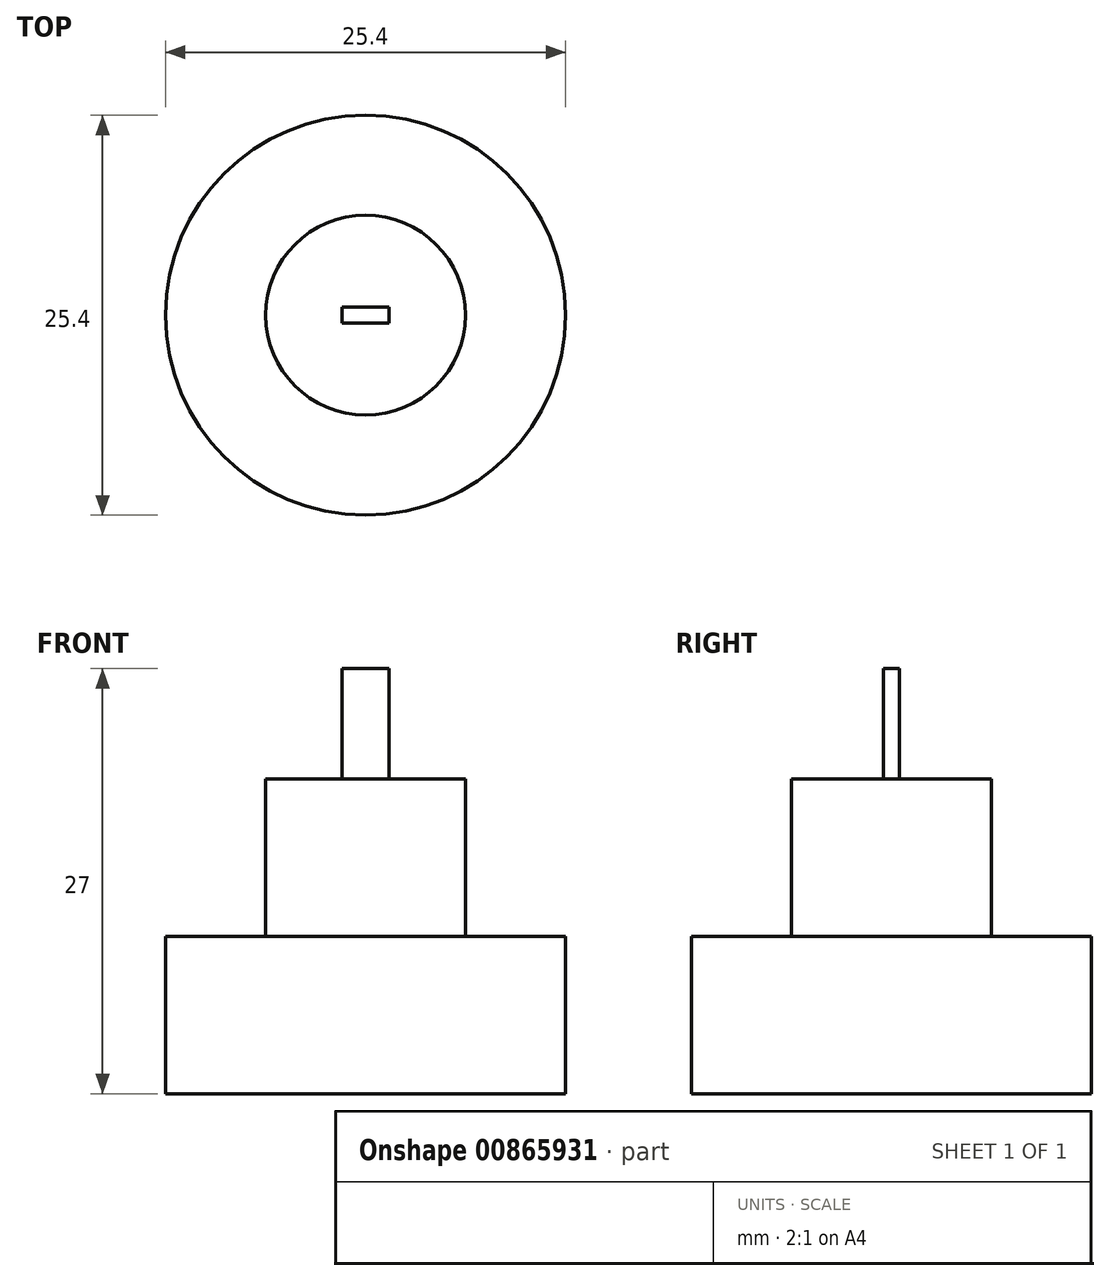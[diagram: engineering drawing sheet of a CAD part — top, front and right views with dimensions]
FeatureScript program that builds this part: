
annotation { "Feature Type Name" : "Feature", "Feature Type Description" : "" }
export const myFeature = defineFeature(function(context is Context, id is Id, definition is map)
    precondition{}
    {
        {
            var Q0;
            Q0=qCreatedBy(makeId("Top.planeOp"),FACE);
            var sketch = newSketch(context, id + "F0", { "sketchPlane" : qUnion([Q0])});
            skCircle(sketch, "E0", {"center": v(0, 0) * mm, "radius": 12.7 * mm});
            skCircle(sketch, "E1", {"center": v(0, 0) * mm, "radius": 6.35 * mm});
            skSolve(sketch);
        }
        {
            var Q0;
            Q0=makeQuery(id+"F0.imprint","IMPRINT",FACE,{"disambiguationData":[TD([[makeQuery(id+"F0.imprint","IMPRINT",EDGE,{"derivedFrom":sQuery(id+"F0.wireOp",EDGE,"E0")}),1.0]])]});
            extrude(context, id + "F1", {"entities" : qUnion([Q0]), "depth" : 10 * mm, "offsetDistance" : 25 * mm});
        }
        {
            var Q0;
            Q0=makeQuery(id+"F0.imprint","IMPRINT",FACE,{"disambiguationData":[TD([[makeQuery(id+"F0.imprint","IMPRINT",EDGE,{"derivedFrom":sQuery(id+"F0.wireOp",EDGE,"E1")}),1.0]])]});
            extrude(context, id + "F2", {"entities" : qUnion([Q0]), "operationType" : NewBodyOperationType.ADD, "depth" : 20 * mm, "offsetDistance" : 25 * mm});
        }
        {
            var Q0;
            Q0=makeQuery(id+"F2.opExtrude","CAP_FACE",FACE,{"disambiguationData":[OSD([sQuery(id+"F0.wireOp",EDGE,"E1")])],"isStart":false});
            var sketch = newSketch(context, id + "F3", { "sketchPlane" : qUnion([Q0])});
            skLineSegment(sketch, "E2.bottom", {"start": v(1.5, 0.5) * mm, "end": v(-1.5, 0.5) * mm});
            skLineSegment(sketch, "E2.top", {"start": v(1.5, -0.5) * mm, "end": v(-1.5, -0.5) * mm});
            skLineSegment(sketch, "E2.left", {"start": v(1.5, 0.5) * mm, "end": v(1.5, -0.5) * mm});
            skLineSegment(sketch, "E2.right", {"start": v(-1.5, 0.5) * mm, "end": v(-1.5, -0.5) * mm});
            skPoint(sketch, "E2.middle", {"position": v(0, 0) * mm});
            skSolve(sketch);
        }
        {
            var Q0;
            Q0=makeQuery(id+"F3.imprint","IMPRINT",FACE,{"disambiguationData":[TD([[makeQuery(id+"F3.imprint","IMPRINT",EDGE,{"derivedFrom":sQuery(id+"F3.wireOp",EDGE,"E2.bottom")}),1.0]])]});
            extrude(context, id + "F4", {"entities" : qUnion([Q0]), "operationType" : NewBodyOperationType.ADD, "depth" : 7 * mm, "offsetDistance" : 25 * mm});
        }
    });
